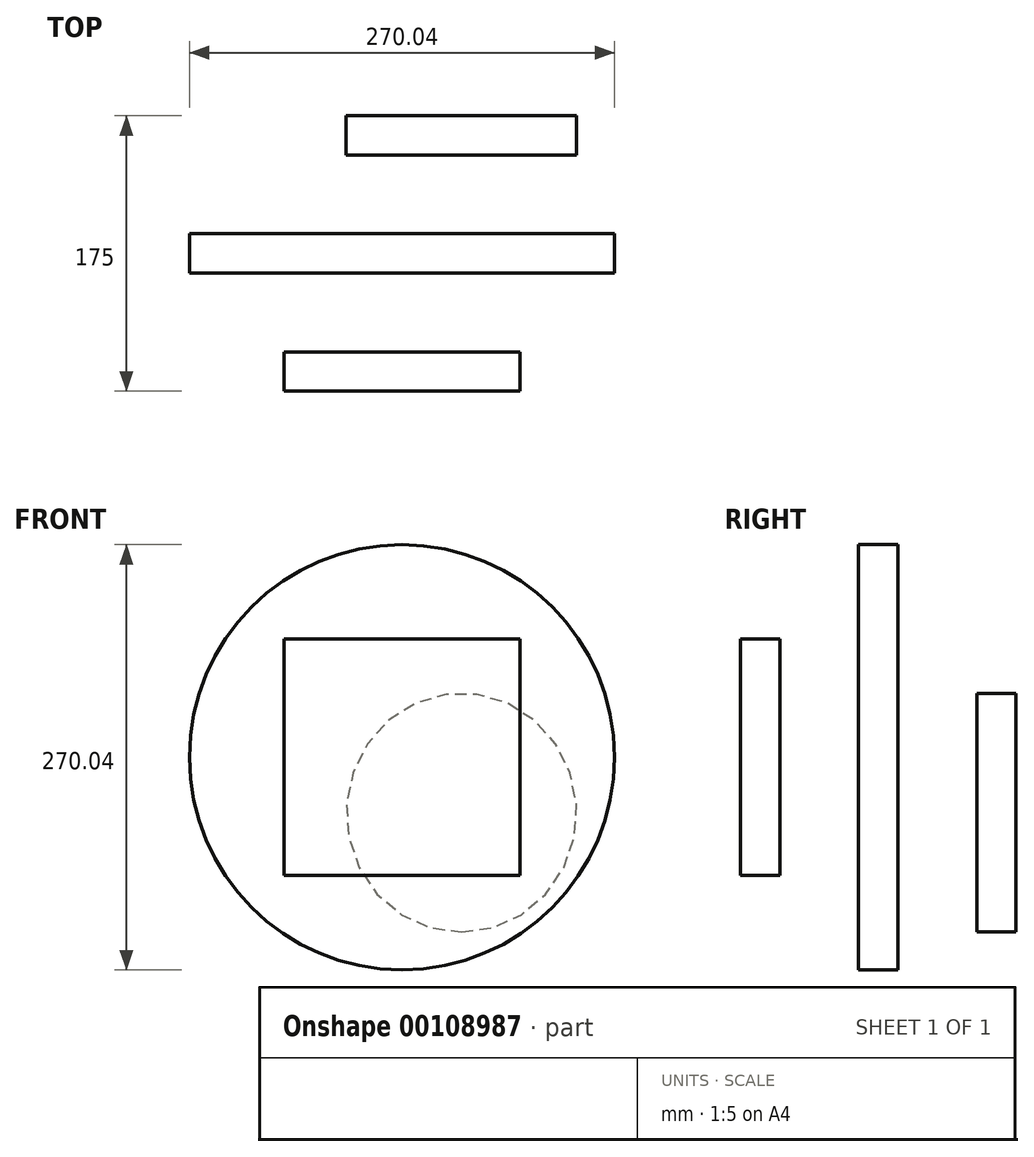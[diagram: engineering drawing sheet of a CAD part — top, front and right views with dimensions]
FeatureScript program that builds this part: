
annotation { "Feature Type Name" : "Feature", "Feature Type Description" : "" }
export const myFeature = defineFeature(function(context is Context, id is Id, definition is map)
    precondition{}
    {
        {
            var Q0;
            Q0=qCreatedBy(makeId("Front.planeOp"),FACE);
            cPlane(context, id + "F0", {"entities" : qUnion([Q0]), "cplaneType" : CPlaneType.OFFSET, "offset" : 75 * mm, "width" : 150 * mm, "height" : 150 * mm});
        }
        {
            var Q0;
            Q0=qCreatedBy(makeId("Front.planeOp"),FACE);
            cPlane(context, id + "F1", {"entities" : qUnion([Q0]), "cplaneType" : CPlaneType.OFFSET, "offset" : 75 * mm, "oppositeDirection" : true, "width" : 150 * mm, "height" : 150 * mm});
        }
        {
            var Q0;
            Q0=qCreatedBy(id+"F0.planeOp",FACE);
            var sketch = newSketch(context, id + "F2", { "sketchPlane" : qUnion([Q0])});
            skLineSegment(sketch, "E0.bottom", {"start": v(75, 75) * mm, "end": v(-75, 75) * mm});
            skLineSegment(sketch, "E0.top", {"start": v(75, -75) * mm, "end": v(-75, -75) * mm});
            skLineSegment(sketch, "E0.left", {"start": v(75, 75) * mm, "end": v(75, -75) * mm});
            skLineSegment(sketch, "E0.right", {"start": v(-75, 75) * mm, "end": v(-75, -75) * mm});
            skPoint(sketch, "E0.middle", {"position": v(0, 0) * mm});
            skSolve(sketch);
        }
        {
            var Q0;
            Q0=qCreatedBy(makeId("Front.planeOp"),FACE);
            var sketch = newSketch(context, id + "F3", { "sketchPlane" : qUnion([Q0])});
            skCircle(sketch, "E1", {"center": v(0, 0) * mm, "radius": 135.02 * mm});
            skSolve(sketch);
        }
        {
            var Q0;
            Q0=qCreatedBy(id+"F1.planeOp",FACE);
            var sketch = newSketch(context, id + "F4", { "sketchPlane" : qUnion([Q0])});
            skEllipse(sketch, "E2", {"center": v(37.8, -35.22) * mm, "majorRadius": 73.19 * mm, "minorRadius": 75.8 * mm, "majorAxis": v(-1, 0)});
            skSolve(sketch);
        }
        {
            var Q0;
            Q0=makeQuery(id+"F2.imprint","IMPRINT",FACE,{"disambiguationData":[TD([[makeQuery(id+"F2.imprint","IMPRINT",EDGE,{"derivedFrom":sQuery(id+"F2.wireOp",EDGE,"E0.bottom")}),1.0]])]});
            var Q1;
            Q1=makeQuery(id+"F3.imprint","IMPRINT",FACE,{"disambiguationData":[TD([[makeQuery(id+"F3.imprint","IMPRINT",EDGE,{"derivedFrom":sQuery(id+"F3.wireOp",EDGE,"E1")}),1.0]])]});
            var Q2;
            Q2=makeQuery(id+"F4.imprint","IMPRINT",FACE,{"disambiguationData":[TD([[makeQuery(id+"F4.imprint","IMPRINT",EDGE,{"derivedFrom":sQuery(id+"F4.wireOp",EDGE,"E2")}),1.0]])]});
            var Q3;
            Q3=qBodyType(qCreatedBy(id+"F4",EDGE),BodyType.WIRE);
            var Q4;
            Q4=sQuery(id+"F3.wireOp",EDGE,"E1");
            var Q5;
            Q5=qBodyType(qCreatedBy(id+"F2",EDGE),BodyType.WIRE);
            extrude(context, id + "F5", {"entities" : qUnion([Q0, Q1, Q2]), "surfaceEntities" : qUnion([Q3, Q4, Q5]), "depth" : 25 * mm});
        }
    });
